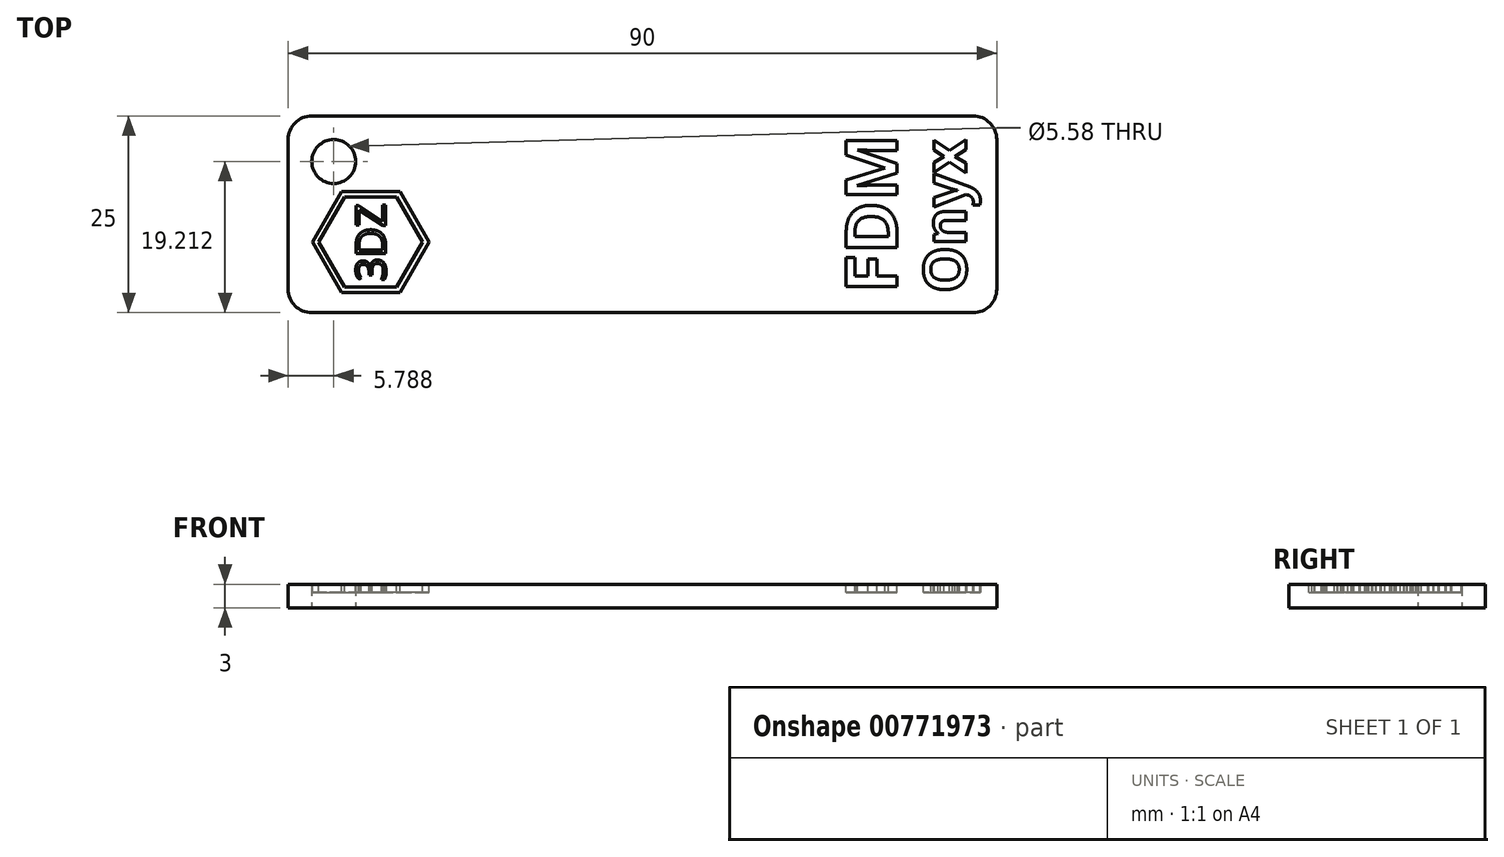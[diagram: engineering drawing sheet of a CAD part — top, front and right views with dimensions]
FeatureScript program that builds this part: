
annotation { "Feature Type Name" : "Feature", "Feature Type Description" : "" }
export const myFeature = defineFeature(function(context is Context, id is Id, definition is map)
    precondition{}
    {
        {
            var Q0;
            Q0=qCreatedBy(makeId("Top.planeOp"),FACE);
            var sketch = newSketch(context, id + "F0", { "sketchPlane" : qUnion([Q0])});
            skLineSegment(sketch, "E0.bottom", {"start": v(-42, 12.5) * mm, "end": v(42, 12.5) * mm});
            skLineSegment(sketch, "E0.top", {"start": v(-42, -12.5) * mm, "end": v(42, -12.5) * mm});
            skLineSegment(sketch, "E0.left", {"start": v(-45, 9.5) * mm, "end": v(-45, -9.5) * mm});
            skLineSegment(sketch, "E0.right", {"start": v(45, 9.5) * mm, "end": v(45, -9.5) * mm});
            skPoint(sketch, "E0.middle", {"position": v(0, 0) * mm});
            skPoint(sketch, "E1.visualSharp", {"position": v(-45, 12.5) * mm});
            skArc(sketch, "E1.filletArc", {"start": v(-42, 12.5) * mm, "mid": v(-44.12, 11.62) * mm, "end": v(-45, 9.5) * mm});
            skPoint(sketch, "E2.visualSharp", {"position": v(45, 12.5) * mm});
            skArc(sketch, "E2.filletArc", {"start": v(45, 9.5) * mm, "mid": v(44.12, 11.62) * mm, "end": v(42, 12.5) * mm});
            skPoint(sketch, "E3.visualSharp", {"position": v(45, -12.5) * mm});
            skArc(sketch, "E3.filletArc", {"start": v(42, -12.5) * mm, "mid": v(44.12, -11.62) * mm, "end": v(45, -9.5) * mm});
            skPoint(sketch, "E4.visualSharp", {"position": v(-45, -12.5) * mm});
            skArc(sketch, "E4.filletArc", {"start": v(-45, -9.5) * mm, "mid": v(-44.12, -11.62) * mm, "end": v(-42, -12.5) * mm});
            skCircle(sketch, "E5", {"center": v(-39.21, 6.71) * mm, "radius": 2.79 * mm});
            skSolve(sketch);
        }
        {
            var Q0;
            Q0=makeQuery(id+"F0.imprint","IMPRINT",FACE,{"disambiguationData":[TD([[makeQuery(id+"F0.imprint","IMPRINT",EDGE,{"derivedFrom":sQuery(id+"F0.wireOp",EDGE,"E0.bottom")}),-1.0]])]});
            extrude(context, id + "F1", {"entities" : qUnion([Q0]), "depth" : 3 * mm, "offsetDistance" : 25 * mm});
        }
        {
            var Q0;
            Q0=makeQuery(id+"F1.opExtrude","CAP_FACE",FACE,{"disambiguationData":[OSD([sQuery(id+"F0.wireOp",EDGE,"E0.bottom"),sQuery(id+"F0.wireOp",EDGE,"E0.top"),sQuery(id+"F0.wireOp",EDGE,"E0.left"),sQuery(id+"F0.wireOp",EDGE,"E0.right"),sQuery(id+"F0.wireOp",EDGE,"E1.filletArc"),sQuery(id+"F0.wireOp",EDGE,"E2.filletArc"),sQuery(id+"F0.wireOp",EDGE,"E3.filletArc"),sQuery(id+"F0.wireOp",EDGE,"E4.filletArc"),sQuery(id+"F0.wireOp",EDGE,"E5")])],"isStart":false});
            var sketch = newSketch(context, id + "F2", { "sketchPlane" : qUnion([Q0])});
            skPoint(sketch, "E6", {"position": v(45, 0) * mm});
            skText(sketch, "E7", { "text": "FDM\n", "fontName": "OpenSans-Bold.ttf"});
            skText(sketch, "E8", { "text": "Onyx\n", "fontName": "OpenSans-Bold.ttf"});
            const initialGuessF2  = {"E7": [0.03235, -0.01, 0, 1, 0.00652], "E8": [0.04112, -0.01, 0, 1, 0.00541]};
            skSetInitialGuess(sketch, initialGuessF2);
            skSolve(sketch);
        }
        {
            var Q0;
            Q0 = qSketchRegion(id + "F2", true);
            extrude(context, id + "F3", {"entities" : qUnion([Q0]), "operationType" : NewBodyOperationType.REMOVE, "oppositeDirection" : true, "depth" : 1 * mm, "offsetDistance" : 25 * mm});
        }
        {
            var Q0;
            {var subQ0=sQuery(id+"F0.wireOp",EDGE,"E0.top");var subQ1=sQuery(id+"F0.wireOp",EDGE,"E0.right");var subQ2=sQuery(id+"F0.wireOp",EDGE,"E0.bottom");var subQ3=sQuery(id+"F0.wireOp",EDGE,"E1.filletArc");var subQ4=sQuery(id+"F0.wireOp",EDGE,"E2.filletArc");var subQ5=sQuery(id+"F0.wireOp",EDGE,"E3.filletArc");var subQ6=sQuery(id+"F0.wireOp",EDGE,"E4.filletArc");var subQ7=sQuery(id+"F0.wireOp",EDGE,"E5");var subQ8=sQuery(id+"F0.wireOp",EDGE,"E0.left");Q0=makeQuery(id+"F3.boolean.opBoolean","SPLIT",FACE,{"disambiguationData":[TD([makeQuery(id+"F1.opExtrude","SWEPT_FACE",FACE,{"disambiguationData":[OSD([subQ2])]})])],"derivedFrom":makeQuery(id+"F1.opExtrude","CAP_FACE",FACE,{"disambiguationData":[OSD([subQ2,subQ0,subQ8,subQ1,subQ3,subQ4,subQ5,subQ6,subQ7])],"isStart":false})});}
            var sketch = newSketch(context, id + "F4", { "sketchPlane" : qUnion([Q0])});
            skText(sketch, "E9", { "text": "3DZ", "fontName": "OpenSans-Regular.ttf"});
            skCircle(sketch, "E10.cCircle", {"center": v(-34.5, -3.5) * mm, "radius": 6.42 * mm, "construction": true});
            skLineSegment(sketch, "E10.0", {"start": v(-41.92, -3.5) * mm, "end": v(-38.21, 2.92) * mm});
            skLineSegment(sketch, "E10.1", {"start": v(-38.21, 2.92) * mm, "end": v(-30.8, 2.91) * mm});
            skLineSegment(sketch, "E10.2", {"start": v(-30.8, 2.91) * mm, "end": v(-27.1, -3.5) * mm});
            skLineSegment(sketch, "E10.3", {"start": v(-27.1, -3.5) * mm, "end": v(-30.8, -9.92) * mm});
            skLineSegment(sketch, "E10.4", {"start": v(-30.8, -9.92) * mm, "end": v(-38.22, -9.92) * mm});
            skLineSegment(sketch, "E10.5", {"start": v(-38.22, -9.92) * mm, "end": v(-41.92, -3.5) * mm});
            skPoint(sketch, "E10.0.midPoint", {"position": v(-40.07, -0.3) * mm});
            skLineSegment(sketch, "E11.0", {"start": v(-31.2, -9.22) * mm, "end": v(-37.81, -9.22) * mm});
            skLineSegment(sketch, "E11.1", {"start": v(-41.11, -3.5) * mm, "end": v(-37.8, 2.22) * mm});
            skLineSegment(sketch, "E11.2", {"start": v(-37.8, 2.22) * mm, "end": v(-31.2, 2.21) * mm});
            skLineSegment(sketch, "E11.3", {"start": v(-37.81, -9.22) * mm, "end": v(-41.11, -3.5) * mm});
            skLineSegment(sketch, "E11.4", {"start": v(-31.2, 2.21) * mm, "end": v(-27.9, -3.5) * mm});
            skLineSegment(sketch, "E11.5", {"start": v(-27.9, -3.5) * mm, "end": v(-31.2, -9.22) * mm});
            const initialGuessF4  = {"E9": [-0.03261, -0.0085, 0, 1, 0.0038]};
            skSetInitialGuess(sketch, initialGuessF4);
            skSolve(sketch);
        }
        {
            var Q0;
            Q0 = qSketchRegion(id + "F4", true);
            var Q1;
            Q1=makeQuery(id+"F4.imprint","IMPRINT",FACE,{"disambiguationData":[TD([[makeQuery(id+"F4.imprint","IMPRINT",EDGE,{"derivedFrom":sQuery(id+"F4.wireOp",EDGE,"E9.sketch_text.stroke-42")}),-1.0]])]});
            var Q2;
            Q2=makeQuery(id+"F4.imprint","IMPRINT",FACE,{"disambiguationData":[TD([[makeQuery(id+"F4.imprint","IMPRINT",EDGE,{"derivedFrom":sQuery(id+"F4.wireOp",EDGE,"E9.sketch_text.stroke-28")}),-1.0]])]});
            var Q3;
            Q3=makeQuery(id+"F4.imprint","IMPRINT",FACE,{"disambiguationData":[TD([[makeQuery(id+"F4.imprint","IMPRINT",EDGE,{"derivedFrom":sQuery(id+"F4.wireOp",EDGE,"E9.sketch_text.stroke-0")}),-1.0]])]});
            var Q4;
            Q4 = qConstructionFilter(qBodyType(qCreatedBy(id + "F4" ,EDGE), BodyType.WIRE), ConstructionObject.NO);
            extrude(context, id + "F5", {"entities" : qUnion([Q0, Q1, Q2, Q3]), "operationType" : NewBodyOperationType.REMOVE, "surfaceEntities" : qUnion([Q4]), "oppositeDirection" : true, "depth" : 1 * mm, "offsetDistance" : 25 * mm});
        }
    });
